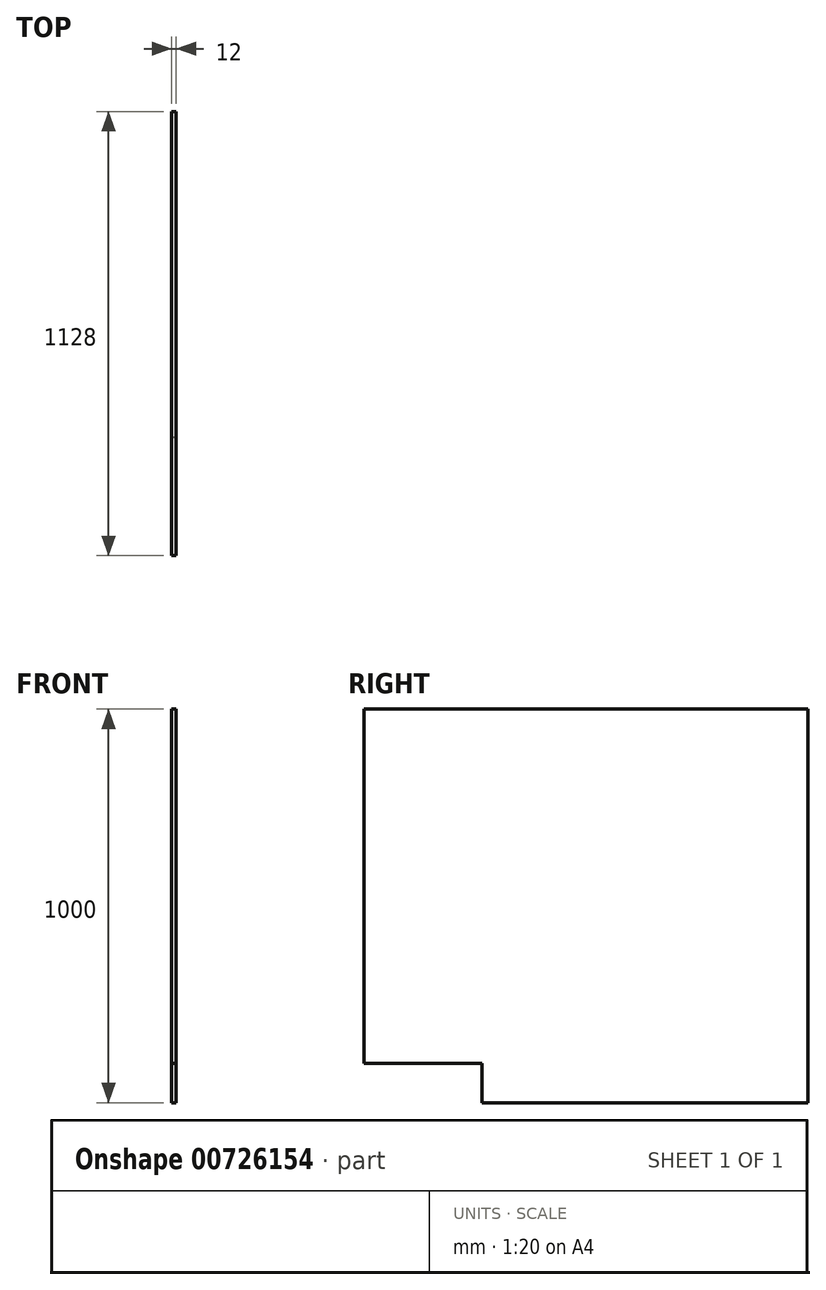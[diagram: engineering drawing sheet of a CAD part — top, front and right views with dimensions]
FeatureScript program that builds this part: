
annotation { "Feature Type Name" : "Feature", "Feature Type Description" : "" }
export const myFeature = defineFeature(function(context is Context, id is Id, definition is map)
    precondition{}
    {
        {
            var Q0;
            Q0=qCreatedBy(makeId("Right.planeOp"),FACE);
            var sketch = newSketch(context, id + "F0", { "sketchPlane" : qUnion([Q0])});
            skLineSegment(sketch, "E0.bottom", {"start": v(-564, 500) * mm, "end": v(564, 500) * mm});
            skLineSegment(sketch, "E0.top", {"start": v(-264, -500) * mm, "end": v(564, -500) * mm});
            skLineSegment(sketch, "E0.left", {"start": v(-564, 500) * mm, "end": v(-564, -400) * mm});
            skLineSegment(sketch, "E0.right", {"start": v(564, 500) * mm, "end": v(564, -500) * mm});
            skLineSegment(sketch, "E1", {"start": v(0, 500) * mm, "end": v(0, -500) * mm, "construction": true});
            skLineSegment(sketch, "E2", {"start": v(-264, -500) * mm, "end": v(-264, -400) * mm});
            skLineSegment(sketch, "E3", {"start": v(-264, -400) * mm, "end": v(-564, -400) * mm});
            skPoint(sketch, "E4.orphan", {"position": v(-564, -500) * mm});
            skSolve(sketch);
        }
        {
            var Q0;
            Q0 = qSketchRegion(id + "F0", true);
            extrude(context, id + "F1", {"entities" : qUnion([Q0]), "depth" : 12 * mm, "offsetDistance" : 25 * mm});
        }
    });
